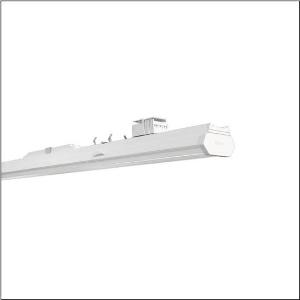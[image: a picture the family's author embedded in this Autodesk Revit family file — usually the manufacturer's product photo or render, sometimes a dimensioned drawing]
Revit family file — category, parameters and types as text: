
# Revit family: licross_11_protected_mo_51td12dn495g3s
name_source: partatom
category: Lighting Fixtures
units: mm (PartAtom-declared; Revit-internal decimal feet)

## family parameters
Cut with Voids When Loaded = No
Host = Face
Light Source = No
Part Type = Normal
Room Calculation Point = No
Round Connector Dimension = Use Diameter
Shared = No

## types (1)
- --- (1 x LED, 980 lm, 6.8 W, 4000K)
    Apparent Load = 7 VA
    CIE Flux Codes = 73 92 98 99 100
    Color Rendering = 80
    Color Temperature = 4000K
    Default Elevation = 1800 mm
    Description = Licross 11 Protected MO, luminaire insert, of sheet steel, galvanised, coil coated, white, length: 1.500mm, width: 90mm, height: 101mm, LED rated luminous flux: 9.980lm, light colour: 840, SDCM (Standard Deviation of Colour Matching)MacAdam ≤ 2 SDCM (initial), control gear: DALI 2 (for two DALI lines), with plug, 6-pole, with phase selection, for trunking rail, 14-core, mains connection: 220..240V, AC, 50/60Hz, rated input power: 61W, for trunking rail, 14-core, internal wiring halogen-free, for emergency light function, converter,control gear: single battery element, battery: LiFePO4, 9Ah, primary light control with lens, of plastic, primary optical cover: cover, of PMMA, light emission: direct distribution, primary light characteristic: symmetric, protection rating (complete): IP54, insulation class (complete): insulation class I (protective earthing), certification: CE, UKCA, protection symbol: D if used in an environment with non-conductive dust loads with corresponding accessories, impact resistance: IK06, permissible ambient temperature for indoor applications: +5..+35°C, standard: EN 60598-2-22, LABS conformity tested according to VDMA 24364:2018-05, reducing of maximum allowable ambient temperature of 5°C with ceiling mounting, corresponds to IFS (International Featured Standards) requirements for safety and quality in the food industry, The light source and the operating device comply with the requirements of the Ecodesign Regulation (EU) 2019/2020 and are replaceable in accordance with this regulation, packaging unit: 1 piece
    Height = 92 mm
    Lamp = 1 x LED
    Lamp Light Flux = 980 lm
    Lamp Power = 6.8 W
    Lamp count = 1
    Length = 1500 mm
    Luminous efficacy = 144 lm/W
    Manufacturer = Siteco
    ModVariant = No
    Model = 51TD12DN495G3S
    Mounting Place = Ceiling
    Mounting Type = Pendant
    Number of Poles = 1
    OnlyDefault = Yes
    Power Factor = 1
    Product Name = Licross 11 Protected MO
    Product group = luminaire insert | ceiling pendant
    ProductGroupID = 901
    Protection Class = Protection class I
    Protection Degree = IP 54
    RLX_Detail_Level = 1
    RLX_Emergency_Light_Flux = 0 lm
    RLX_Emergency_Type = 0
    RLX_Emergency_Type_DB = No
    RlxData = <blob elided: 25021 chars, md5=4c4953d6>
    Socket = socket
    Standby Power = 0 W
    System Light Flux = 980 lm
    System Power = 7 W
    Type Comments = : emergency light operation: 3 h
    Type Image = l_1256145.jpg
    URL = http://relux.com
    VarID = @adj_096169
    Voltage = 0 V
    Weight = 0.00 kg
    Width = 88 mm

## geometry (parser evidence)
native form markers: Blend x4, Sweep x9
no freeform markers — native parametric forms only
